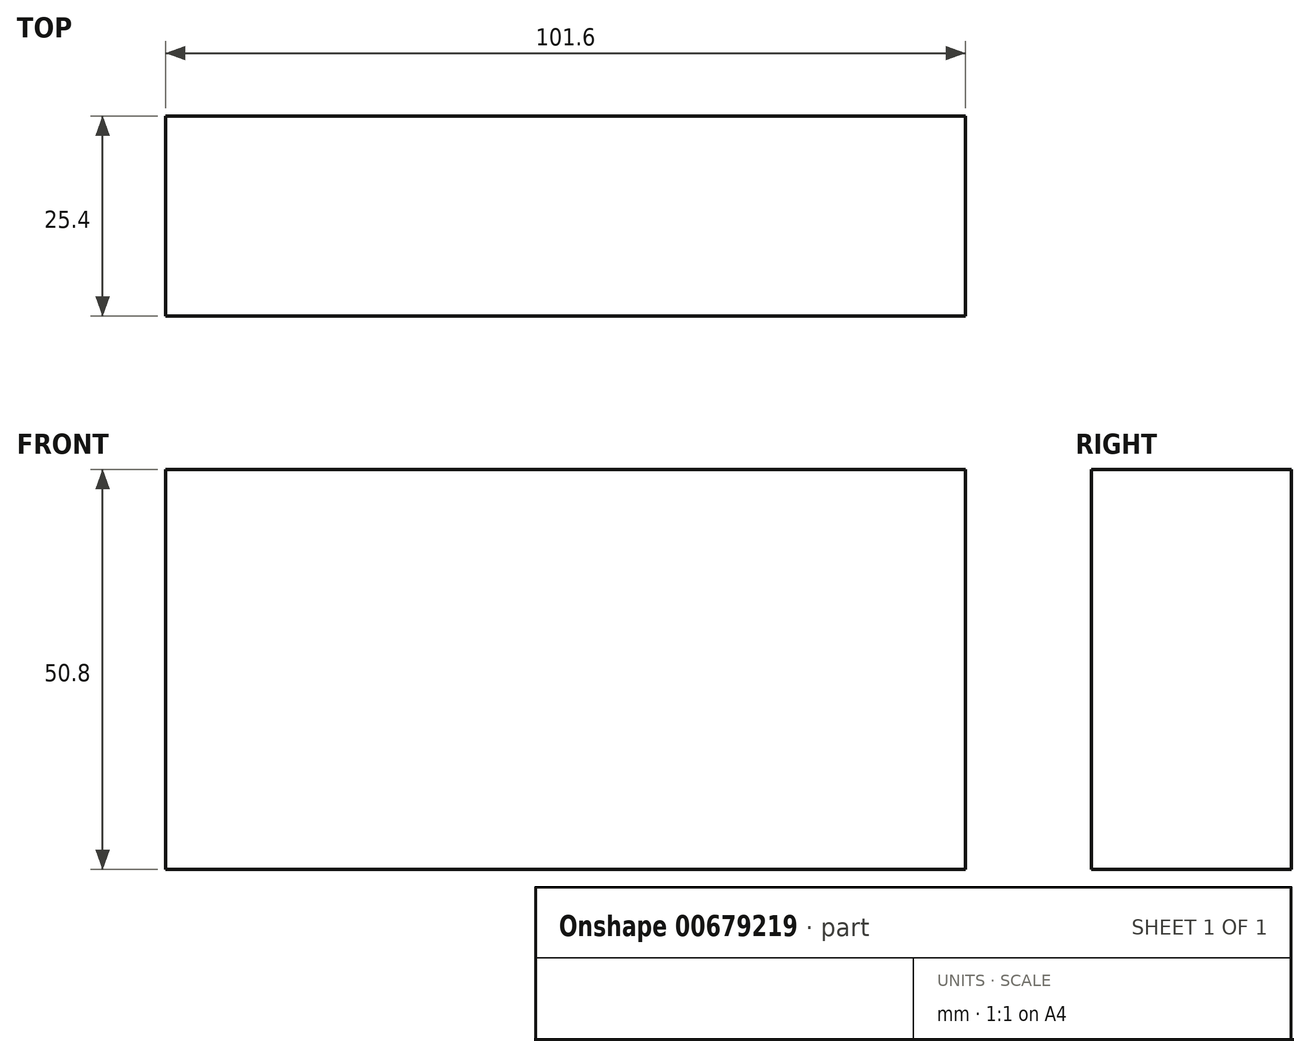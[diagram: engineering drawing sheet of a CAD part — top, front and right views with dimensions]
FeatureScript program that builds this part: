
annotation { "Feature Type Name" : "Feature", "Feature Type Description" : "" }
export const myFeature = defineFeature(function(context is Context, id is Id, definition is map)
    precondition{}
    {
        {
            var Q0;
            Q0=qCreatedBy(makeId("Front.planeOp"),FACE);
            var sketch = newSketch(context, id + "F0", { "sketchPlane" : qUnion([Q0])});
            skLineSegment(sketch, "E0.bottom", {"start": v(-50.8, 25.4) * mm, "end": v(50.8, 25.4) * mm});
            skLineSegment(sketch, "E0.top", {"start": v(-50.8, -25.4) * mm, "end": v(50.8, -25.4) * mm});
            skLineSegment(sketch, "E0.left", {"start": v(-50.8, 25.4) * mm, "end": v(-50.8, -25.4) * mm});
            skLineSegment(sketch, "E0.right", {"start": v(50.8, 25.4) * mm, "end": v(50.8, -25.4) * mm});
            skPoint(sketch, "E0.middle", {"position": v(0, 0) * mm});
            skSolve(sketch);
        }
        {
            var Q0;
            Q0=makeQuery(id+"F0.imprint","IMPRINT",FACE,{"disambiguationData":[TD([[makeQuery(id+"F0.imprint","IMPRINT",EDGE,{"derivedFrom":sQuery(id+"F0.wireOp",EDGE,"E0.bottom")}),-1.0]])]});
            extrude(context, id + "F1", {"entities" : qUnion([Q0]), "depth" : 25.4 * mm, "offsetDistance" : 25.4 * mm});
        }
    });
